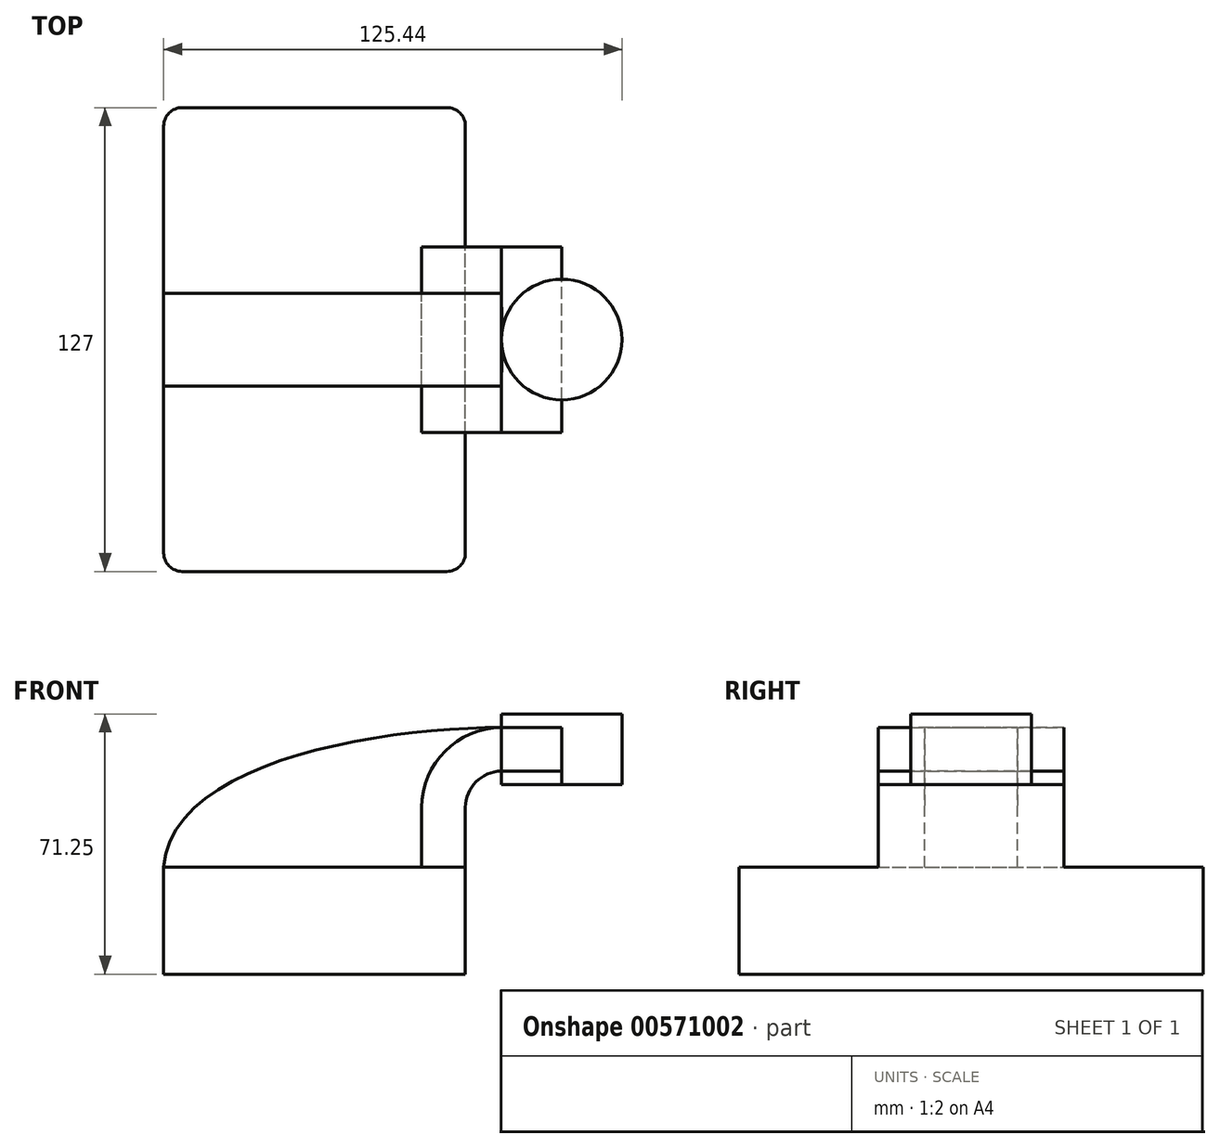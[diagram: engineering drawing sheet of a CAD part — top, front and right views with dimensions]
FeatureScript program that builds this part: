
annotation { "Feature Type Name" : "Feature", "Feature Type Description" : "" }
export const myFeature = defineFeature(function(context is Context, id is Id, definition is map)
    precondition{}
    {
        {
            var Q0;
            Q0=qCreatedBy(makeId("Front.planeOp"),FACE);
            var sketch = newSketch(context, id + "F0", { "sketchPlane" : qUnion([Q0])});
            skLineSegment(sketch, "E0.bottom", {"start": v(41.28, -14.64) * mm, "end": v(-41.28, -14.64) * mm});
            skLineSegment(sketch, "E0.top", {"start": v(41.28, 14.64) * mm, "end": v(-41.28, 14.64) * mm});
            skLineSegment(sketch, "E0.left", {"start": v(41.28, -14.64) * mm, "end": v(41.28, 14.64) * mm});
            skLineSegment(sketch, "E0.right", {"start": v(-41.28, -14.64) * mm, "end": v(-41.28, 14.64) * mm});
            skPoint(sketch, "E0.middle", {"position": v(0, 0) * mm});
            skLineSegment(sketch, "E1.bottom", {"start": v(84.16, 37.24) * mm, "end": v(51.14, 37.24) * mm});
            skLineSegment(sketch, "E1.top", {"start": v(84.16, 56.6) * mm, "end": v(51.14, 56.6) * mm});
            skLineSegment(sketch, "E1.left", {"start": v(84.16, 37.24) * mm, "end": v(84.16, 56.6) * mm});
            skLineSegment(sketch, "E1.right", {"start": v(51.14, 37.24) * mm, "end": v(51.14, 56.6) * mm});
            skPoint(sketch, "E1.middle", {"position": v(67.65, 46.92) * mm});
            skLineSegment(sketch, "E2", {"start": v(41.28, 14.64) * mm, "end": v(41.28, 30.98) * mm});
            skArc(sketch, "E3", {"start": v(41.27, 30.98) * mm, "mid": v(44.2, 38.02) * mm, "end": v(51.23, 40.94) * mm});
            skLineSegment(sketch, "E4", {"start": v(51.23, 40.94) * mm, "end": v(67.65, 40.94) * mm});
            skLineSegment(sketch, "E5.0", {"start": v(51.23, 52.89) * mm, "end": v(67.65, 52.89) * mm});
            skArc(sketch, "E5.1", {"start": v(29.33, 30.98) * mm, "mid": v(35.74, 46.47) * mm, "end": v(51.23, 52.89) * mm});
            skLineSegment(sketch, "E5.2", {"start": v(29.33, 14.64) * mm, "end": v(29.33, 30.98) * mm});
            skLineSegment(sketch, "E6", {"start": v(67.65, 37.24) * mm, "end": v(67.65, 56.6) * mm});
            skFitSpline(sketch, "E7", {"points": [v(-41.28, 14.64) * mm, v(51.23, 52.89) * mm], "startDerivative": vector(6.03, 87.02) * mm, "endDerivative": vector(100.45, 0.15) * mm});
            skSolve(sketch);
        }
        {
            var Q0;
            {var subQ5=sQuery(id+"F0.wireOp",EDGE,"E2");Q0=makeQuery(id+"F0.imprint","IMPRINT",FACE,{"disambiguationData":[TD([[makeQuery(id+"F0.imprint","IMPRINT",EDGE,{"derivedFrom":subQ5}),1.0]])]});}
            var Q1;
            {var subQ0=sQuery(id+"F0.wireOp",EDGE,"E4");var subQ1=sQuery(id+"F0.wireOp",EDGE,"E1.right");var subQ2=makeQuery(id+"F0.imprint","INTERSECT",VERTEX,{"derivedFrom":[subQ1,subQ0]});Q1=makeQuery(id+"F0.imprint","IMPRINT",FACE,{"disambiguationData":[TD([[makeQuery(id+"F0.imprint","IMPRINT",EDGE,{"disambiguationData":[TD([[subQ2,-1.0]])],"derivedFrom":subQ1}),-1.0]])]});}
            extrude(context, id + "F1", {"entities" : qUnion([Q0, Q1]), "endBound" : BoundingType.SYMMETRIC, "depth" : 50.8 * mm, "offsetDistance" : 25.4 * mm});
        }
        {
            var Q0;
            Q0=makeQuery(id+"F0.imprint","IMPRINT",FACE,{"disambiguationData":[TD([[makeQuery(id+"F0.imprint","IMPRINT",EDGE,{"derivedFrom":sQuery(id+"F0.wireOp",EDGE,"E0.bottom")}),-1.0]])]});
            extrude(context, id + "F2", {"entities" : qUnion([Q0]), "operationType" : NewBodyOperationType.ADD, "endBound" : BoundingType.SYMMETRIC, "depth" : 127 * mm, "offsetDistance" : 25.4 * mm});
        }
        {
            var Q0;
            {var subQ4=sQuery(id+"F0.wireOp",EDGE,"E5.1");Q0=makeQuery(id+"F0.imprint","IMPRINT",FACE,{"disambiguationData":[TD([[makeQuery(id+"F0.imprint","IMPRINT",EDGE,{"derivedFrom":subQ4}),1.0]])]});}
            extrude(context, id + "F3", {"entities" : qUnion([Q0]), "operationType" : NewBodyOperationType.ADD, "endBound" : BoundingType.SYMMETRIC, "depth" : 17.78 * mm, "offsetDistance" : 25.4 * mm});
        }
        {
            var Q0;
            {var subQ4=sQuery(id+"F0.wireOp",EDGE,"E1.left");Q0=makeQuery(id+"F0.imprint","IMPRINT",FACE,{"disambiguationData":[TD([[makeQuery(id+"F0.imprint","IMPRINT",EDGE,{"derivedFrom":subQ4}),1.0]])]});}
            var Q1;
            Q1=sQuery(id+"F0.wireOp",EDGE,"E6");
            revolve(context, id + "F4", {"operationType" : NewBodyOperationType.ADD, "entities" : qUnion([Q0]), "axis" : qUnion([Q1]), "revolveType" : RevolveType.FULL});
        }
        {
            var Q0;
            {var subQ1=sQuery(id+"F0.wireOp",EDGE,"E4");Q0=makeQuery(id+"F0.imprint","IMPRINT",FACE,{"disambiguationData":[TD([[makeQuery(id+"F0.imprint","IMPRINT",EDGE,{"derivedFrom":subQ1}),1.0]])]});}
            extrude(context, id + "F5", {"entities" : qUnion([Q0]), "endBound" : BoundingType.SYMMETRIC, "depth" : 50.8 * mm, "offsetDistance" : 25.4 * mm});
        }
        {
            var Q0;
            {var subQ0=sQuery(id+"F0.wireOp",EDGE,"E5.2");Q0=makeQuery(id+"F0.imprint","IMPRINT",FACE,{"disambiguationData":[TD([[makeQuery(id+"F0.imprint","IMPRINT",EDGE,{"derivedFrom":subQ0}),1.0]])]});}
            extrude(context, id + "F6", {"entities" : qUnion([Q0]), "endBound" : BoundingType.SYMMETRIC, "depth" : 25.4 * mm, "offsetDistance" : 25.4 * mm});
        }
        {
            var Q0;
            Q0=makeQuery(id+"F2.opExtrude","CAP_EDGE",EDGE,{"disambiguationData":[OSD([sQuery(id+"F0.wireOp",EDGE,"E0.right")])],"isStart":false});
            var Q1;
            Q1=makeQuery(id+"F2.opExtrude","CAP_EDGE",EDGE,{"disambiguationData":[OSD([sQuery(id+"F0.wireOp",EDGE,"E0.left")])],"isStart":false});
            var Q2;
            Q2=makeQuery(id+"F2.opExtrude","CAP_EDGE",EDGE,{"disambiguationData":[OSD([sQuery(id+"F0.wireOp",EDGE,"E0.right")])],"isStart":true});
            var Q3;
            Q3=makeQuery(id+"F2.opExtrude","CAP_EDGE",EDGE,{"disambiguationData":[OSD([sQuery(id+"F0.wireOp",EDGE,"E0.left")])],"isStart":true});
            fillet(context, id + "F7", {"entities" : qUnion([Q0, Q1, Q2, Q3]), "radius" : 5.08 * mm, "tangentPropagation" : true, "allowEdgeOverflow" : false});
        }
    });
